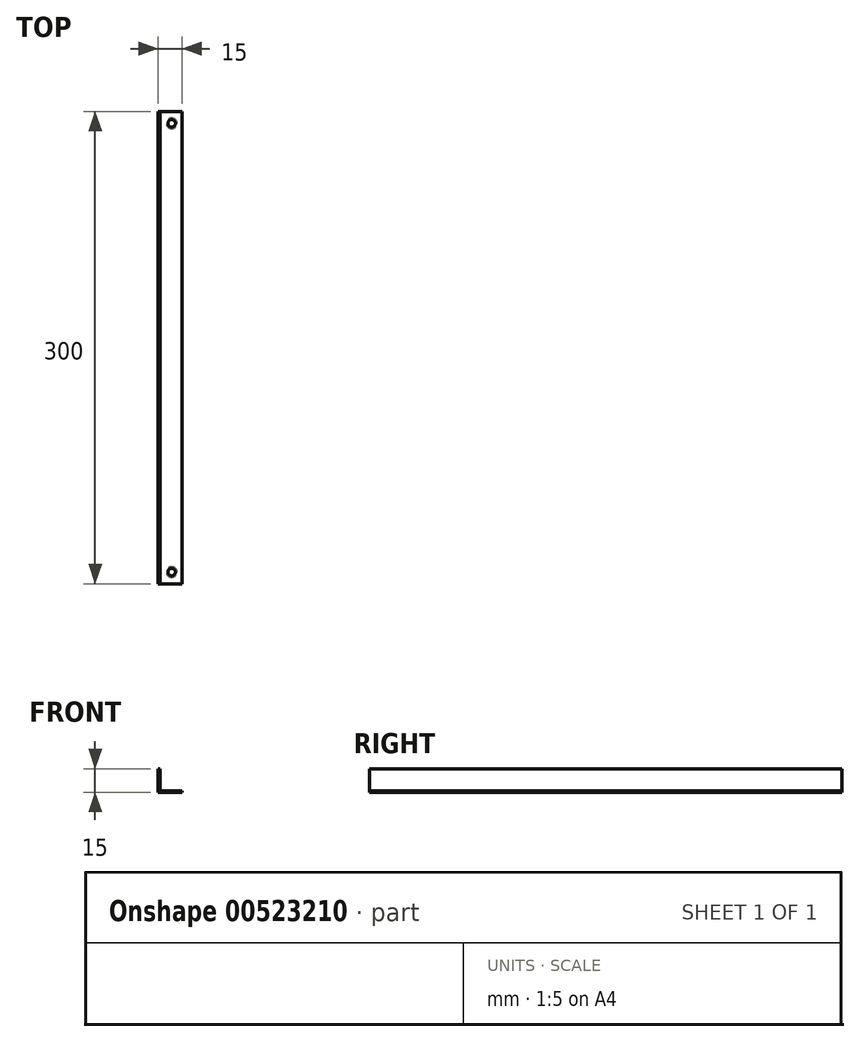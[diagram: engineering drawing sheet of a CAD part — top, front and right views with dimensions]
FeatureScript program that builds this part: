
annotation { "Feature Type Name" : "Feature", "Feature Type Description" : "" }
export const myFeature = defineFeature(function(context is Context, id is Id, definition is map)
    precondition{}
    {
        {
            var Q0;
            Q0=qCreatedBy(makeId("Front.planeOp"),FACE);
            var sketch = newSketch(context, id + "F0", { "sketchPlane" : qUnion([Q0])});
            skLineSegment(sketch, "E0", {"start": v(-16.03, 8.98) * mm, "end": v(-16.03, -6.02) * mm});
            skLineSegment(sketch, "E1", {"start": v(-16.03, -6.02) * mm, "end": v(-1.03, -6.02) * mm});
            skLineSegment(sketch, "E2", {"start": v(-1.03, -6.02) * mm, "end": v(-1.03, -5.02) * mm});
            skLineSegment(sketch, "E3", {"start": v(-1.03, -5.02) * mm, "end": v(-15.03, -5.02) * mm});
            skLineSegment(sketch, "E4", {"start": v(-15.03, -5.02) * mm, "end": v(-15.03, 8.98) * mm});
            skLineSegment(sketch, "E5", {"start": v(-15.03, 8.98) * mm, "end": v(-16.03, 8.98) * mm});
            skSolve(sketch);
        }
        {
            var Q0;
            Q0=makeQuery(id+"F0.imprint","IMPRINT",FACE,{"disambiguationData":[TD([[makeQuery(id+"F0.imprint","IMPRINT",EDGE,{"derivedFrom":sQuery(id+"F0.wireOp",EDGE,"E0")}),1.0]])]});
            extrude(context, id + "F1", {"entities" : qUnion([Q0]), "depth" : 300 * mm, "offsetDistance" : 25 * mm});
        }
        {
            var Q0;
            Q0=makeQuery(id+"F1.opExtrude","SWEPT_FACE",FACE,{"disambiguationData":[OSD([sQuery(id+"F0.wireOp",EDGE,"E1")])]});
            var sketch = newSketch(context, id + "F2", { "sketchPlane" : qUnion([Q0])});
            skLineSegment(sketch, "E6", {"start": v(-16.03, 292.5) * mm, "end": v(-1.03, 292.5) * mm, "construction": true});
            skLineSegment(sketch, "E7", {"start": v(-7.53, 300) * mm, "end": v(-7.53, 292.5) * mm, "construction": true});
            skLineSegment(sketch, "E8", {"start": v(-7.53, 292.5) * mm, "end": v(-7.53, 0) * mm, "construction": true});
            skLineSegment(sketch, "E9", {"start": v(-1.03, 7.5) * mm, "end": v(-16.03, 7.5) * mm, "construction": true});
            skPoint(sketch, "E10", {"position": v(-7.53, 7.5) * mm});
            skPoint(sketch, "E11", {"position": v(-7.53, 292.5) * mm});
            skSolve(sketch);
        }
        {
            var Q0;
            Q0=sQuery(id+"F2.wireOp",VERTEX,"E11");
            var Q1;
            Q1=sQuery(id+"F2.wireOp",VERTEX,"E10");
            var Q2;
            Q2=makeQuery(id+"F1.opExtrude","SWEPT_BODY",BODY,{"disambiguationData":[OSD([sQuery(id+"F0.wireOp",EDGE,"E0"),sQuery(id+"F0.wireOp",EDGE,"E1"),sQuery(id+"F0.wireOp",EDGE,"E2"),sQuery(id+"F0.wireOp",EDGE,"E3"),sQuery(id+"F0.wireOp",EDGE,"E4"),sQuery(id+"F0.wireOp",EDGE,"E5")])]});
            hole(context, id + "F3", {"style" : HoleStyle.C_SINK, "endStyle" : HoleEndStyle.THROUGH, "standardTappedOrClearance" : lookupTablePath({ "standard" : "ISO", "engagement" : "75%", "pitch" : "0.5 mm", "size" : "M3", "type" : "Tapped" }), "standardBlindInLast" : lookupTablePath({ "standard" : "ISO", "engagement" : "75%", "pitch" : "0.5 mm", "size" : "M3", "type" : "Tapped" }), "holeDiameter" : 2.5 * mm, "cSinkDiameter" : 6.72 * mm, "cSinkAngle" : 90 * degree, "showTappedDepth" : true, "isTappedThrough" : true, "tappedDepth" : 12 * mm, "tapClearance" : 3, "startFromSketch" : true, "locations" : qUnion([Q0, Q1]), "scope" : qUnion([Q2]), "majorDiameter" : 3 * mm});
        }
    });
